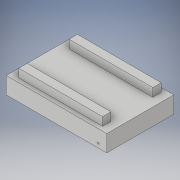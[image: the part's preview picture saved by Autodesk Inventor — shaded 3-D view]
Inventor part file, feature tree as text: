
AUTODESK INVENTOR PART (.ipt)
format: ipt  version: 2019 (Build 230136000, 136)  size: 125,952 bytes
history: native  units: in
note: dims shown in document units (in); Inventor stores cm internally (conversion verified against a paired STEP export)
features: sketch x3, extrude x2, plane x1, hole x1
ambient origin geometry x8: Origin, YZ Plane, XZ Plane, XY Plane, X Axis, Y Axis, Z Axis, Center Point
bodies: Solid1 (feature_tree)
feature tree (7):
  extrude  "Extrusion1"  Depth=4.0in
  plane  "Work Plane1"
  extrude  "Extrusion3"  Depth=0.25in
  hole  "Hole1"  [1 undecoded]
  sketch  "Sketch1"  dims[d0=6.0in d1=4.0in]
  sketch  "Sketch3"  dims[d2=1.5in d3=0.0in d12=0.25in]
  sketch  "Sketch4"  dims[d13=0.5in d14=0.5in d15=0.5in d16=0.5in d17=0.0in d18=0.5in d19=0.25in d20=0.1in d21=0.75in d22=0.375in d23=0.25in d24=0.5635in d25=1.0in d26=0.8108in]
note: 1 required parameter value undecoded (feature->parameter linkage not recoverable at this tier; creation-order binding heuristic only, values carry confidence <= 0.55)
